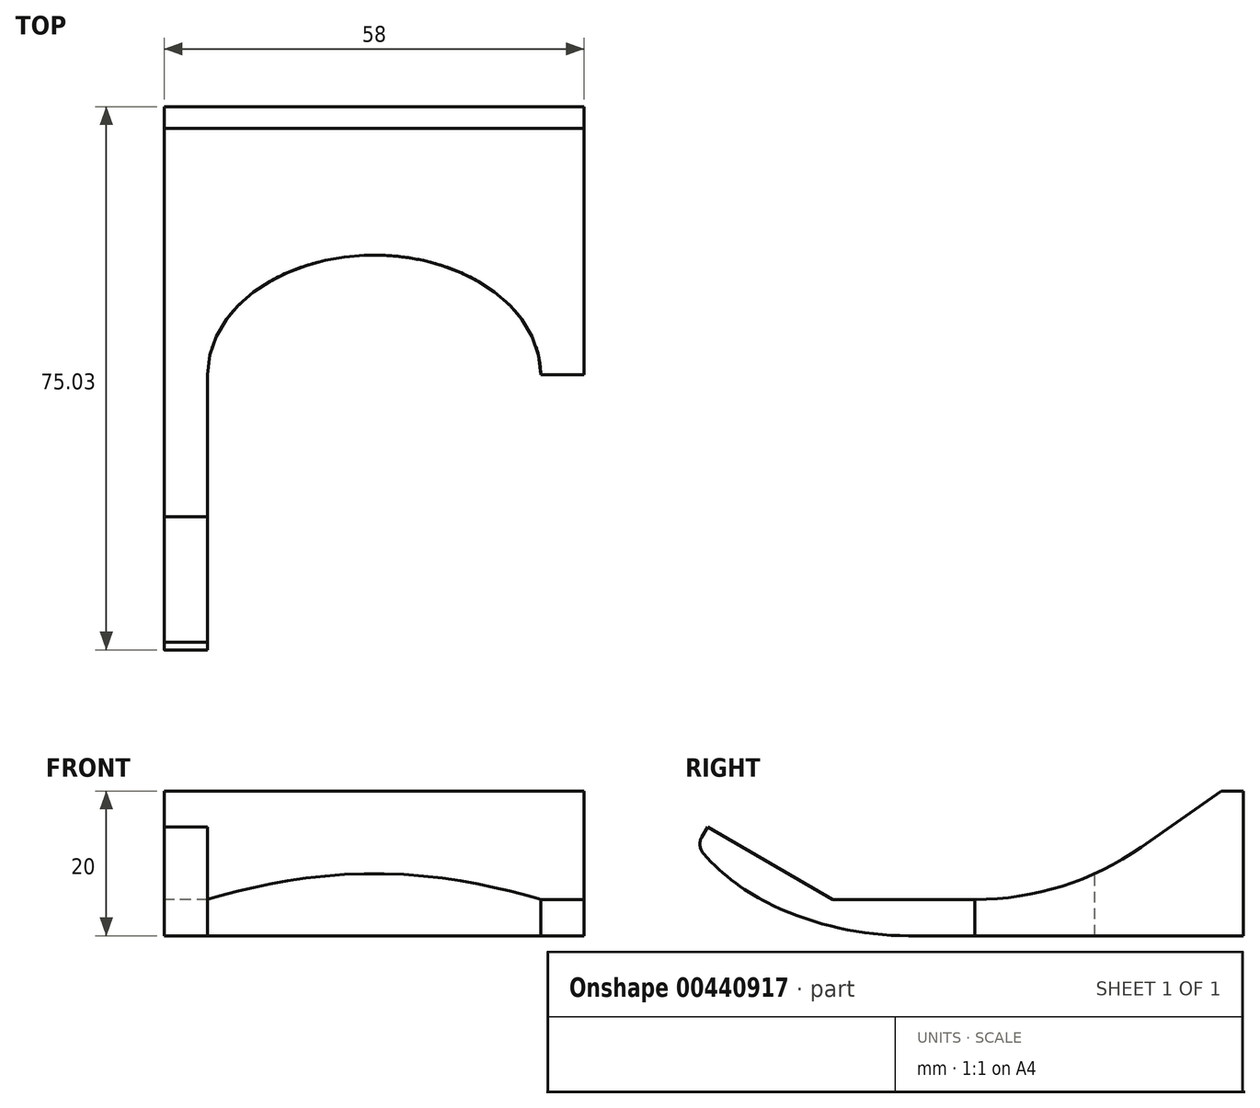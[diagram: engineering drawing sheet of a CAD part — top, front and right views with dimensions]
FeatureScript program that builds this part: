
annotation { "Feature Type Name" : "Feature", "Feature Type Description" : "" }
export const myFeature = defineFeature(function(context is Context, id is Id, definition is map)
    precondition{}
    {
        {
            var Q0;
            Q0=qCreatedBy(makeId("Front.planeOp"),FACE);
            var sketch = newSketch(context, id + "F0", { "sketchPlane" : qUnion([Q0])});
            skLineSegment(sketch, "E0.bottom", {"start": v(-29, 10) * mm, "end": v(29, 10) * mm});
            skLineSegment(sketch, "E0.top", {"start": v(-29, -10) * mm, "end": v(29, -10) * mm});
            skLineSegment(sketch, "E0.left", {"start": v(-29, 10) * mm, "end": v(-29, -10) * mm});
            skLineSegment(sketch, "E0.right", {"start": v(29, 10) * mm, "end": v(29, -10) * mm});
            skPoint(sketch, "E0.middle", {"position": v(0, 0) * mm});
            skSolve(sketch);
        }
        {
            var Q0;
            Q0 = qSketchRegion(id + "F0", true);
            extrude(context, id + "F1", {"entities" : qUnion([Q0]), "depth" : 8 * mm});
        }
        {
            var Q0;
            Q0=makeQuery(id+"F1.opExtrude","CAP_EDGE",EDGE,{"disambiguationData":[OSD([sQuery(id+"F0.wireOp",EDGE,"E0.bottom")])],"isStart":false});
            chamfer(context, id + "F2", {"entities" : qUnion([Q0]), "chamferType" : ChamferType.TWO_OFFSETS, "width1" : 5 * mm, "oppositeDirection" : false, "width2" : 3.5 * mm, "tangentPropagation" : true});
        }
        {
            var Q0;
            Q0=makeQuery(id+"F1.opExtrude","CAP_FACE",FACE,{"disambiguationData":[OSD([sQuery(id+"F0.wireOp",EDGE,"E0.bottom"),sQuery(id+"F0.wireOp",EDGE,"E0.top"),sQuery(id+"F0.wireOp",EDGE,"E0.left"),sQuery(id+"F0.wireOp",EDGE,"E0.right")])],"isStart":false});
            var sketch = newSketch(context, id + "F3", { "sketchPlane" : qUnion([Q0])});
            skLineSegment(sketch, "E1", {"start": v(-23, -10) * mm, "end": v(-23, 28.83) * mm, "construction": true});
            skLineSegment(sketch, "E2", {"start": v(20, -10) * mm, "end": v(20, 24.92) * mm, "construction": true});
            skLineSegment(sketch, "E3.bottom", {"start": v(-29, -10) * mm, "end": v(-23, -10) * mm});
            skLineSegment(sketch, "E3.top", {"start": v(-29, -5) * mm, "end": v(-23, -5) * mm});
            skLineSegment(sketch, "E3.left", {"start": v(-29, -10) * mm, "end": v(-29, -5) * mm});
            skLineSegment(sketch, "E3.right", {"start": v(-23, -10) * mm, "end": v(-23, -5) * mm});
            skSolve(sketch);
        }
        {
            var Q0;
            Q0 = qSketchRegion(id + "F3", true);
            extrude(context, id + "F4", {"entities" : qUnion([Q0]), "operationType" : NewBodyOperationType.ADD, "depth" : 50 * mm});
        }
        {
            var Q0;
            Q0=makeQuery(id+"F4.boolean.opBoolean","MERGE",FACE,{"derivedFrom":[makeQuery(id+"F1.opExtrude","SWEPT_FACE",FACE,{"disambiguationData":[OSD([sQuery(id+"F0.wireOp",EDGE,"E0.left")])]}),makeQuery(id+"F4.opExtrude","SWEPT_FACE",FACE,{"disambiguationData":[OSD([sQuery(id+"F3.wireOp",EDGE,"E3.left")])]})]});
            var sketch = newSketch(context, id + "F5", { "sketchPlane" : qUnion([Q0])});
            skLineSegment(sketch, "E4", {"start": v(58, -10) * mm, "end": v(76.48, 0.67) * mm});
            skLineSegment(sketch, "E5", {"start": v(76.48, 0.67) * mm, "end": v(73.98, 5) * mm});
            skLineSegment(sketch, "E6", {"start": v(73.98, 5) * mm, "end": v(56.66, -5) * mm});
            skLineSegment(sketch, "E7", {"start": v(56.66, -5) * mm, "end": v(58, -10) * mm});
            skSolve(sketch);
        }
        {
            var Q0;
            Q0 = qSketchRegion(id + "F5", true);
            var Q1;
            Q1=makeQuery(id+"F4.opExtrude","SWEPT_FACE",FACE,{"disambiguationData":[OSD([sQuery(id+"F3.wireOp",EDGE,"E3.right")])]});
            extrude(context, id + "F6", {"entities" : qUnion([Q0]), "operationType" : NewBodyOperationType.ADD, "endBound" : BoundingType.UP_TO_SURFACE, "oppositeDirection" : true, "endBoundEntityFace" : qUnion([Q1]), "depth" : 25 * mm});
        }
        {
            var Q0;
            Q0=makeQuery(id+"F6.opExtrude","SWEPT_EDGE",EDGE,{"disambiguationData":[OSD([sQuery(id+"F5.wireOp",EDGE,"E4"),sQuery(id+"F5.wireOp",EDGE,"E5")])]});
            chamfer(context, id + "F7", {"entities" : qUnion([Q0]), "chamferType" : ChamferType.TWO_OFFSETS, "width1" : 6 * mm, "oppositeDirection" : false, "width2" : 2 * mm, "tangentPropagation" : true});
        }
        {
            var Q0;
            Q0=makeQuery(id+"F6.opExtrude","SWEPT_EDGE",EDGE,{"disambiguationData":[OSD([sQuery(id+"F0.wireOp",EDGE,"E0.left"),sQuery(id+"F3.wireOp",EDGE,"E3.top"),sQuery(id+"F3.wireOp",EDGE,"E3.left"),sQuery(id+"F5.wireOp",EDGE,"E6"),sQuery(id+"F5.wireOp",EDGE,"E7")])]});
            var Q1;
            {var subQ0=sQuery(id+"F3.wireOp",EDGE,"E3.bottom");Q1=makeQuery(id+"F6.boolean.opBoolean","MERGE",EDGE,{"derivedFrom":[makeQuery(id+"F4.opExtrude","CAP_EDGE",EDGE,{"disambiguationData":[OSD([subQ0])],"isStart":false}),makeQuery(id+"F6.opExtrude","SWEPT_EDGE",EDGE,{"disambiguationData":[OSD([sQuery(id+"F0.wireOp",EDGE,"E0.top"),sQuery(id+"F0.wireOp",EDGE,"E0.left"),subQ0,sQuery(id+"F3.wireOp",EDGE,"E3.left"),sQuery(id+"F5.wireOp",EDGE,"E4"),sQuery(id+"F5.wireOp",EDGE,"E7")])]})]});}
            fillet(context, id + "F8", {"entities" : qUnion([Q0, Q1]), "radius" : 44 * mm, "tangentPropagation" : true, "allowEdgeOverflow" : false});
        }
        {
            var Q0;
            {var subQ0=sQuery(id+"F5.wireOp",EDGE,"E5");Q0=makeQuery(id+"F7.opChamfer","BLEND_EDGE",EDGE,{"blendedFrom":[makeQuery(id+"F6.opExtrude","SWEPT_EDGE",EDGE,{"disambiguationData":[OSD([sQuery(id+"F5.wireOp",EDGE,"E4"),subQ0])]}),makeQuery(id+"F6.opExtrude","SWEPT_FACE",FACE,{"disambiguationData":[OSD([subQ0])]})],"blendedInto":[makeQuery(id+"F6.opExtrude","SWEPT_FACE",FACE,{"disambiguationData":[OSD([subQ0])]})]});}
            fillet(context, id + "F9", {"entities" : qUnion([Q0]), "radius" : 2 * mm, "tangentPropagation" : true, "allowEdgeOverflow" : false});
        }
        {
            var Q0;
            {var subQ0=sQuery(id+"F5.wireOp",EDGE,"E4");Q0=makeQuery(id+"F7.opChamfer","BLEND_EDGE",EDGE,{"blendedFrom":[makeQuery(id+"F6.opExtrude","SWEPT_EDGE",EDGE,{"disambiguationData":[OSD([subQ0,sQuery(id+"F5.wireOp",EDGE,"E5")])]}),makeQuery(id+"F6.opExtrude","SWEPT_FACE",FACE,{"disambiguationData":[OSD([subQ0])]})],"blendedInto":[makeQuery(id+"F6.opExtrude","SWEPT_FACE",FACE,{"disambiguationData":[OSD([subQ0])]})]});}
            fillet(context, id + "F10", {"entities" : qUnion([Q0]), "radius" : 30 * mm, "tangentPropagation" : true, "allowEdgeOverflow" : false});
        }
        {
            var Q0;
            {var subQ0=sQuery(id+"F3.wireOp",EDGE,"E3.right");Q0=makeQuery(id+"F6.boolean.opBoolean","MERGE",FACE,{"derivedFrom":[makeQuery(id+"F4.opExtrude","SWEPT_FACE",FACE,{"disambiguationData":[OSD([subQ0])]}),makeQuery(id+"F6.opExtrude","CAP_FACE",FACE,{"disambiguationData":[OSD([subQ0])],"isStart":false})]});}
            var sketch = newSketch(context, id + "F11", { "sketchPlane" : qUnion([Q0])});
            skLineSegment(sketch, "E8", {"start": v(-8, 6.5) * mm, "end": v(-24.43, -5) * mm, "construction": true});
            skLineSegment(sketch, "E9", {"start": v(-8, -10) * mm, "end": v(-8, 6.5) * mm});
            skCircle(sketch, "E10", {"center": v(-37.04, 35) * mm, "radius": 40 * mm, "construction": true});
            skLineSegment(sketch, "E11", {"start": v(-37.04, 35) * mm, "end": v(-37.04, -5) * mm, "construction": true});
            skArc(sketch, "E12", {"start": v(-37.04, -5) * mm, "mid": v(-25.01, -3.15) * mm, "end": v(-14.1, 2.23) * mm});
            skLineSegment(sketch, "E13", {"start": v(-8, 6.5) * mm, "end": v(-14.1, 2.23) * mm});
            skLineSegment(sketch, "E14", {"start": v(-37.04, -5) * mm, "end": v(-37.04, -10) * mm});
            skLineSegment(sketch, "E15", {"start": v(-37.04, -10) * mm, "end": v(-8, -10) * mm});
            skSolve(sketch);
        }
        {
            var Q0;
            Q0 = qSketchRegion(id + "F11", true);
            var Q1;
            Q1=makeQuery(id+"FctEVZiXP5p4fex_1.1.F6.boolean.opBoolean","MERGE",FACE,{"derivedFrom":[makeQuery(id+"FctEVZiXP5p4fex_1.1.F4.boolean.opBoolean","MERGE",FACE,{"derivedFrom":[makeQuery(id+"F1.opExtrude","SWEPT_FACE",FACE,{"disambiguationData":[OSD([sQuery(id+"F0.wireOp",EDGE,"E0.right")])]}),makeQuery(id+"FctEVZiXP5p4fex_1.1.F4.opExtrude","SWEPT_FACE",FACE,{"disambiguationData":[OSD([sQuery(id+"F3.wireOp",EDGE,"E3.left")])]})]}),makeQuery(id+"FctEVZiXP5p4fex_1.1.F6.opExtrude","CAP_FACE",FACE,{"disambiguationData":[OSD([sQuery(id+"F5.wireOp",EDGE,"E4"),sQuery(id+"F5.wireOp",EDGE,"E5"),sQuery(id+"F5.wireOp",EDGE,"E6"),sQuery(id+"F5.wireOp",EDGE,"E7")])],"isStart":true})]});
            var Q2;
            Q2=makeQuery(id+"F6.boolean.opBoolean","MERGE",FACE,{"derivedFrom":[makeQuery(id+"F4.boolean.opBoolean","MERGE",FACE,{"derivedFrom":[makeQuery(id+"F1.opExtrude","SWEPT_FACE",FACE,{"disambiguationData":[OSD([sQuery(id+"F0.wireOp",EDGE,"E0.left")])]}),makeQuery(id+"F4.opExtrude","SWEPT_FACE",FACE,{"disambiguationData":[OSD([sQuery(id+"F3.wireOp",EDGE,"E3.left")])]})]}),makeQuery(id+"F6.opExtrude","CAP_FACE",FACE,{"disambiguationData":[OSD([sQuery(id+"F5.wireOp",EDGE,"E4"),sQuery(id+"F5.wireOp",EDGE,"E5"),sQuery(id+"F5.wireOp",EDGE,"E6"),sQuery(id+"F5.wireOp",EDGE,"E7")])],"isStart":true})]});
            extrude(context, id + "F12", {"entities" : qUnion([Q0]), "operationType" : NewBodyOperationType.ADD, "endBound" : BoundingType.UP_TO_SURFACE, "endBoundEntityFace" : qUnion([Q1]), "depth" : 25 * mm, "hasSecondDirection" : true, "secondDirectionBound" : SecondDirectionBoundingType.UP_TO_SURFACE, "secondDirectionOppositeDirection" : true, "secondDirectionBoundEntityFace" : qUnion([Q2]), "secondDirectionDepth" : 25 * mm});
        }
        {
            var Q0;
            {var subQ0=sQuery(id+"F3.wireOp",EDGE,"E3.bottom");Q0=makeQuery(id+"F12.boolean.opBoolean","MERGE",FACE,{"derivedFrom":[makeQuery(id+"FctEVZiXP5p4fex_1.1.F4.boolean.opBoolean","MERGE",FACE,{"derivedFrom":[makeQuery(id+"F4.boolean.opBoolean","MERGE",FACE,{"derivedFrom":[makeQuery(id+"F1.opExtrude","SWEPT_FACE",FACE,{"disambiguationData":[OSD([sQuery(id+"F0.wireOp",EDGE,"E0.top")])]}),makeQuery(id+"F4.opExtrude","SWEPT_FACE",FACE,{"disambiguationData":[OSD([subQ0])]})]}),makeQuery(id+"FctEVZiXP5p4fex_1.1.F4.opExtrude","SWEPT_FACE",FACE,{"disambiguationData":[OSD([subQ0])]})]}),makeQuery(id+"F12.opExtrude","SWEPT_FACE",FACE,{"disambiguationData":[OSD([sQuery(id+"F11.wireOp",EDGE,"E15")])]})]});}
            var sketch = newSketch(context, id + "F13", { "sketchPlane" : qUnion([Q0])});
            skCircle(sketch, "E16", {"center": v(0, 39) * mm, "radius": 18.5 * mm, "construction": true});
            skLineSegment(sketch, "E17", {"start": v(0, 0) * mm, "end": v(0, 39) * mm, "construction": true});
            skEllipse(sketch, "E18", {"center": v(0, 37.04) * mm, "majorRadius": 23 * mm, "minorRadius": 16.54 * mm, "majorAxis": v(-1, 0)});
            skPoint(sketch, "E19", {"position": v(0, 20.5) * mm});
            skSolve(sketch);
        }
        {
            var Q0;
            Q0 = qSketchRegion(id + "F13", true);
            extrude(context, id + "F14", {"entities" : qUnion([Q0]), "operationType" : NewBodyOperationType.REMOVE, "oppositeDirection" : true, "depth" : 25 * mm});
        }
    });
